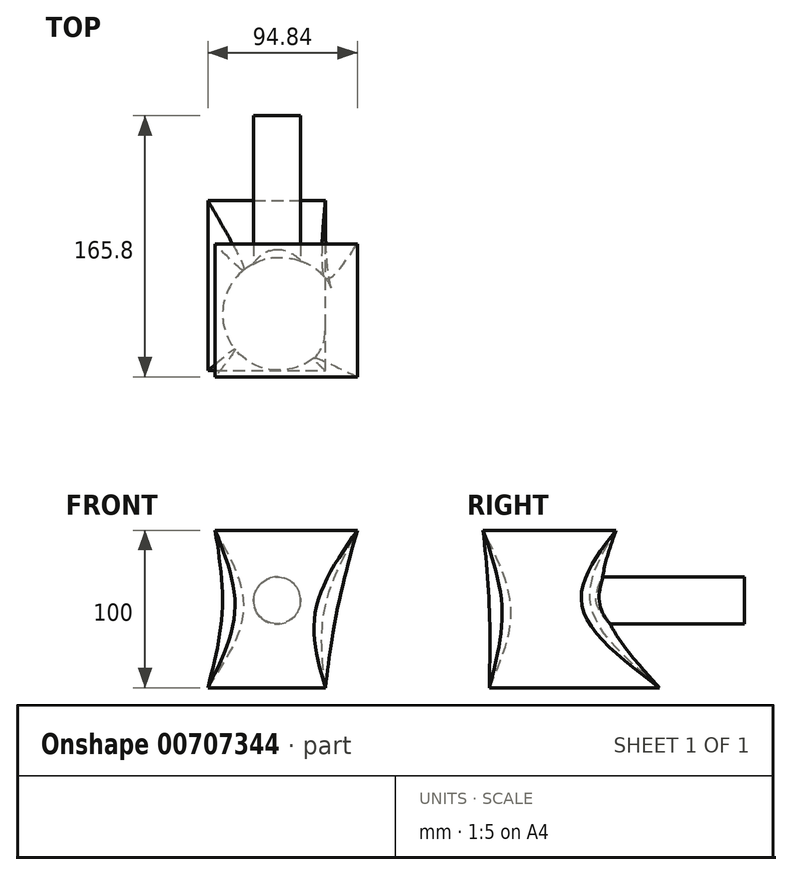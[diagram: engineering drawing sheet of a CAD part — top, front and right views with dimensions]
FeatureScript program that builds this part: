
annotation { "Feature Type Name" : "Feature", "Feature Type Description" : "" }
export const myFeature = defineFeature(function(context is Context, id is Id, definition is map)
    precondition{}
    {
        {
            var Q0;
            Q0=qCreatedBy(makeId("Top.planeOp"),FACE);
            var sketch = newSketch(context, id + "F0", { "sketchPlane" : qUnion([Q0])});
            skCircle(sketch, "E0", {"center": v(-25.55, -25.37) * mm, "radius": 36.5 * mm});
            skSolve(sketch);
        }
        {
            var Q0;
            Q0=qCreatedBy(makeId("Top.planeOp"),FACE);
            cPlane(context, id + "F1", {"entities" : qUnion([Q0]), "cplaneType" : CPlaneType.OFFSET, "offset" : 50 * mm, "width" : 150 * mm, "height" : 150 * mm});
        }
        {
            var Q0;
            Q0=qCreatedBy(id+"F1.planeOp",FACE);
            var sketch = newSketch(context, id + "F2", { "sketchPlane" : qUnion([Q0])});
            skLineSegment(sketch, "E1.bottom", {"start": v(-66.67, -65.8) * mm, "end": v(23.62, -65.8) * mm});
            skLineSegment(sketch, "E1.top", {"start": v(-66.67, 18.55) * mm, "end": v(23.62, 18.55) * mm});
            skLineSegment(sketch, "E1.left", {"start": v(-66.67, -65.8) * mm, "end": v(-66.67, 18.55) * mm});
            skLineSegment(sketch, "E1.right", {"start": v(23.62, -65.8) * mm, "end": v(23.62, 18.55) * mm});
            skSolve(sketch);
        }
        {
            var Q0;
            Q0=qCreatedBy(makeId("Top.planeOp"),FACE);
            cPlane(context, id + "F3", {"entities" : qUnion([Q0]), "cplaneType" : CPlaneType.OFFSET, "offset" : 50 * mm, "oppositeDirection" : true, "width" : 150 * mm, "height" : 150 * mm});
        }
        {
            var Q0;
            Q0=qCreatedBy(id+"F3.planeOp",FACE);
            var sketch = newSketch(context, id + "F4", { "sketchPlane" : qUnion([Q0])});
            skLineSegment(sketch, "E2.bottom", {"start": v(-71.22, -61.95) * mm, "end": v(3.32, -61.95) * mm});
            skLineSegment(sketch, "E2.top", {"start": v(-71.22, 46.2) * mm, "end": v(3.32, 46.2) * mm});
            skLineSegment(sketch, "E2.left", {"start": v(-71.22, -61.95) * mm, "end": v(-71.22, 46.2) * mm});
            skLineSegment(sketch, "E2.right", {"start": v(3.32, -61.95) * mm, "end": v(3.32, 46.2) * mm});
            skSolve(sketch);
        }
        {
            var Q0;
            Q0=makeQuery(id+"F4.imprint","IMPRINT",FACE,{"disambiguationData":[TD([[makeQuery(id+"F4.imprint","IMPRINT",EDGE,{"derivedFrom":sQuery(id+"F4.wireOp",EDGE,"E2.bottom")}),1.0]])]});
            var Q1;
            Q1=makeQuery(id+"F0.imprint","IMPRINT",FACE,{"disambiguationData":[TD([[makeQuery(id+"F0.imprint","IMPRINT",EDGE,{"derivedFrom":sQuery(id+"F0.wireOp",EDGE,"E0")}),1.0]])]});
            var Q2;
            Q2=makeQuery(id+"F2.imprint","IMPRINT",FACE,{"disambiguationData":[TD([[makeQuery(id+"F2.imprint","IMPRINT",EDGE,{"derivedFrom":sQuery(id+"F2.wireOp",EDGE,"E1.bottom")}),1.0]])]});
            loft(context, id + "F5", {"sheetProfilesArray" : [{ "sheetProfileEntities" : qUnion([Q0]) }, { "sheetProfileEntities" : qUnion([Q1]) }, { "sheetProfileEntities" : qUnion([Q2]) }]});
        }
        {
            var Q0;
            Q0=qCreatedBy(makeId("Front.planeOp"),FACE);
            var sketch = newSketch(context, id + "F6", { "sketchPlane" : qUnion([Q0])});
            skCircle(sketch, "E3", {"center": v(-27.3, 5.42) * mm, "radius": 15 * mm});
            skSolve(sketch);
        }
        {
            var Q0;
            Q0 = qSketchRegion(id + "F6", true);
            extrude(context, id + "F7", {"entities" : qUnion([Q0]), "operationType" : NewBodyOperationType.ADD, "oppositeDirection" : true, "depth" : 100 * mm, "offsetDistance" : 25 * mm});
        }
    });
